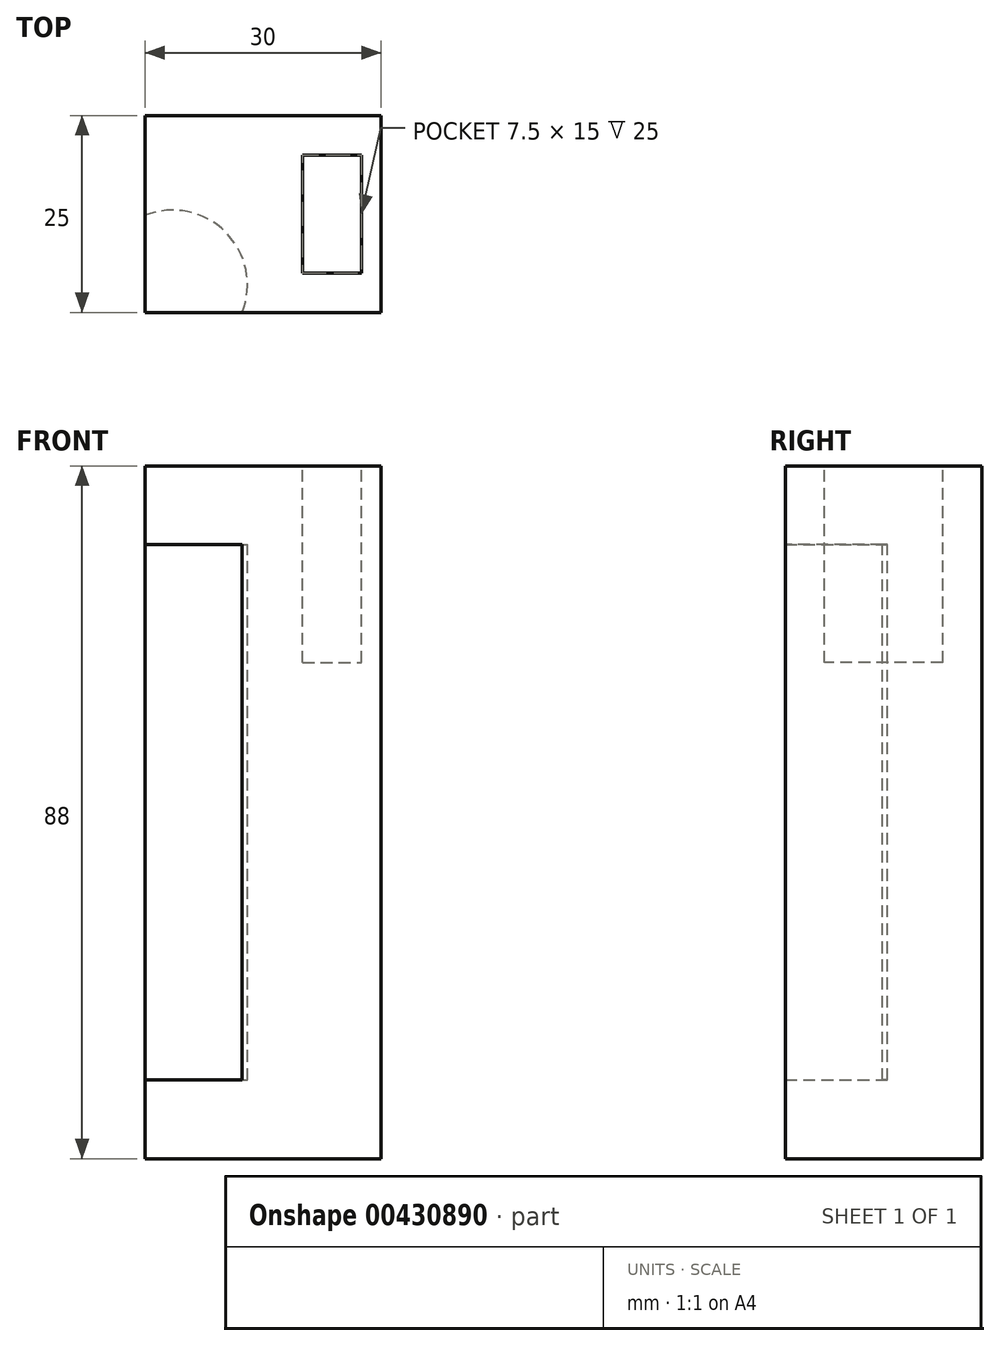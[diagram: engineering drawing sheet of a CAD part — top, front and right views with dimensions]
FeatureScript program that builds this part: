
annotation { "Feature Type Name" : "Feature", "Feature Type Description" : "" }
export const myFeature = defineFeature(function(context is Context, id is Id, definition is map)
    precondition{}
    {
        {
            var Q0;
            Q0=qCreatedBy(makeId("Top.planeOp"),FACE);
            var sketch = newSketch(context, id + "F0", { "sketchPlane" : qUnion([Q0])});
            skLineSegment(sketch, "E0.bottom", {"start": v(-15, 15) * mm, "end": v(15, 15) * mm});
            skLineSegment(sketch, "E0.top", {"start": v(-15, -10) * mm, "end": v(15, -10) * mm});
            skLineSegment(sketch, "E0.left", {"start": v(-15, 15) * mm, "end": v(-15, -10) * mm});
            skLineSegment(sketch, "E0.right", {"start": v(15, 15) * mm, "end": v(15, -10) * mm});
            skCircle(sketch, "E1", {"center": v(-11.5, -6.5) * mm, "radius": 9.5 * mm});
            skLineSegment(sketch, "E2.bottom", {"start": v(5, 10) * mm, "end": v(12.5, 10) * mm});
            skLineSegment(sketch, "E2.top", {"start": v(5, -5) * mm, "end": v(12.5, -5) * mm});
            skLineSegment(sketch, "E2.left", {"start": v(5, 10) * mm, "end": v(5, -5) * mm});
            skLineSegment(sketch, "E2.right", {"start": v(12.5, 10) * mm, "end": v(12.5, -5) * mm});
            skSolve(sketch);
        }
        {
            var Q0;
            {var subQ1=sQuery(id+"F0.wireOp",EDGE,"E0.bottom");Q0=makeQuery(id+"F0.imprint","IMPRINT",FACE,{"disambiguationData":[TD([[makeQuery(id+"F0.imprint","IMPRINT",EDGE,{"derivedFrom":subQ1}),-1.0]])]});}
            var Q1;
            Q1=makeQuery(id+"F0.imprint","IMPRINT",FACE,{"disambiguationData":[TD([[makeQuery(id+"F0.imprint","IMPRINT",EDGE,{"derivedFrom":sQuery(id+"F0.wireOp",EDGE,"E2.bottom")}),-1.0]])]});
            extrude(context, id + "F1", {"entities" : qUnion([Q0, Q1]), "oppositeDirection" : true, "depth" : 88 * mm});
        }
        {
            var Q0;
            {var subQ0=sQuery(id+"F0.wireOp",EDGE,"E0.left");var subQ1=sQuery(id+"F0.wireOp",EDGE,"E0.top");var subQ2=makeQuery(id+"F0.imprint","INTERSECT",VERTEX,{"derivedFrom":[subQ1,subQ0]});Q0=makeQuery(id+"F0.imprint","IMPRINT",FACE,{"disambiguationData":[TD([[makeQuery(id+"F0.imprint","IMPRINT",EDGE,{"disambiguationData":[TD([[subQ2,-1.0]])],"derivedFrom":subQ1}),1.0]])]});}
            extrude(context, id + "F2", {"entities" : qUnion([Q0]), "operationType" : NewBodyOperationType.ADD, "oppositeDirection" : true, "depth" : 10 * mm});
        }
        {
            var Q0;
            Q0=makeQuery(id+"F1.opExtrude","CAP_FACE",FACE,{"disambiguationData":[OSD([sQuery(id+"F0.wireOp",EDGE,"E0.bottom"),sQuery(id+"F0.wireOp",EDGE,"E0.top"),sQuery(id+"F0.wireOp",EDGE,"E0.left"),sQuery(id+"F0.wireOp",EDGE,"E0.right"),sQuery(id+"F0.wireOp",EDGE,"E1")])],"isStart":false});
            var sketch = newSketch(context, id + "F3", { "sketchPlane" : qUnion([Q0])});
            skLineSegment(sketch, "E3.bottom", {"start": v(15, 10) * mm, "end": v(-15, 10) * mm});
            skLineSegment(sketch, "E3.top", {"start": v(15, -15) * mm, "end": v(-15, -15) * mm});
            skLineSegment(sketch, "E3.left", {"start": v(15, 10) * mm, "end": v(15, -15) * mm});
            skLineSegment(sketch, "E3.right", {"start": v(-15, 10) * mm, "end": v(-15, -15) * mm});
            skCircle(sketch, "E4", {"center": v(-11.5, 6.5) * mm, "radius": 9.5 * mm});
            skSolve(sketch);
        }
        {
            var Q0;
            {var subQ0=sQuery(id+"F3.wireOp",EDGE,"E4");Q0=makeQuery(id+"F3.imprint","IMPRINT",FACE,{"disambiguationData":[TD([[makeQuery(id+"F3.imprint","IMPRINT",EDGE,{"disambiguationData":[OD(1.0)],"derivedFrom":subQ0}),-1.0]])]});}
            extrude(context, id + "F4", {"entities" : qUnion([Q0]), "operationType" : NewBodyOperationType.ADD, "oppositeDirection" : true, "depth" : 10 * mm});
        }
        {
            var Q0;
            Q0=makeQuery(id+"F0.imprint","IMPRINT",FACE,{"disambiguationData":[TD([[makeQuery(id+"F0.imprint","IMPRINT",EDGE,{"derivedFrom":sQuery(id+"F0.wireOp",EDGE,"E2.bottom")}),-1.0]])]});
            extrude(context, id + "F5", {"entities" : qUnion([Q0]), "operationType" : NewBodyOperationType.REMOVE, "oppositeDirection" : true, "depth" : 25 * mm});
        }
    });
